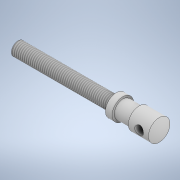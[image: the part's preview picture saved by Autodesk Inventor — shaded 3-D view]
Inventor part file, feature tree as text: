
AUTODESK INVENTOR PART (.ipt)
format: ipt  version: 2021 (Build 250183000, 183)  size: 136,704 bytes
history: native  units: mm
features: other x3, sketch x2, thread x1, extrude x1
ambient origin geometry x8: Origin, YZ Plane, XZ Plane, XY Plane, X Axis, Y Axis, Z Axis, Center Point
bodies: Body1 (feature_tree)
feature tree (7):
  other  "Sólido1"
  other  "Revolução1"
  thread  "Rosca1"  [1 undecoded]
  extrude  "Extrusão1"  Depth=5.0mm
  sketch  "Esboço1"  dims[d2=73.0mm d4=5.0mm]
  sketch  "Esboço2"  dims[d6=12.0mm d8=15.0mm d9=10.0mm d10=16.0mm d11=13.0mm d12=16.0mm d13=90.0deg d14=73.0mm d15=0.0mm d16=6.5mm d17=7.0mm d18=0.0mm d19=0.0mm]
  other  "Projetar arestas de corte1"
note: 1 required parameter value undecoded (feature->parameter linkage not recoverable at this tier; creation-order binding heuristic only, values carry confidence <= 0.55)
